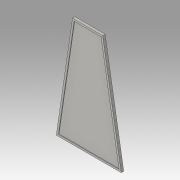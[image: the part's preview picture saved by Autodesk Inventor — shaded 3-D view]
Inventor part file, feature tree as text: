
AUTODESK INVENTOR PART (.ipt)
format: ipt  version: 2016 (Build 200138000, 138)  size: 95,744 bytes
history: native  units: in
note: dims shown in document units (in); Inventor stores cm internally (conversion verified against a paired STEP export)
features: shell x3, extrude x1, sketch x1
ambient origin geometry x8: Origin, YZ Plane, XZ Plane, XY Plane, X Axis, Y Axis, Z Axis, Center Point
bodies: Solid1 (feature_tree)
feature tree (5):
  extrude  "Extrusion1"  Depth=0.02in
  shell  "Shell1"  Thickness=0.135in
  shell  "Shell2"  Thickness=0.1in
  shell  "Shell3"  Thickness=0.05in
  sketch  "Sketch1"  dims[d0=3.5in d1=1.625in d2=0.135in d3=0.0in d4=0.1in d5=0.05in d6=0.02in]
